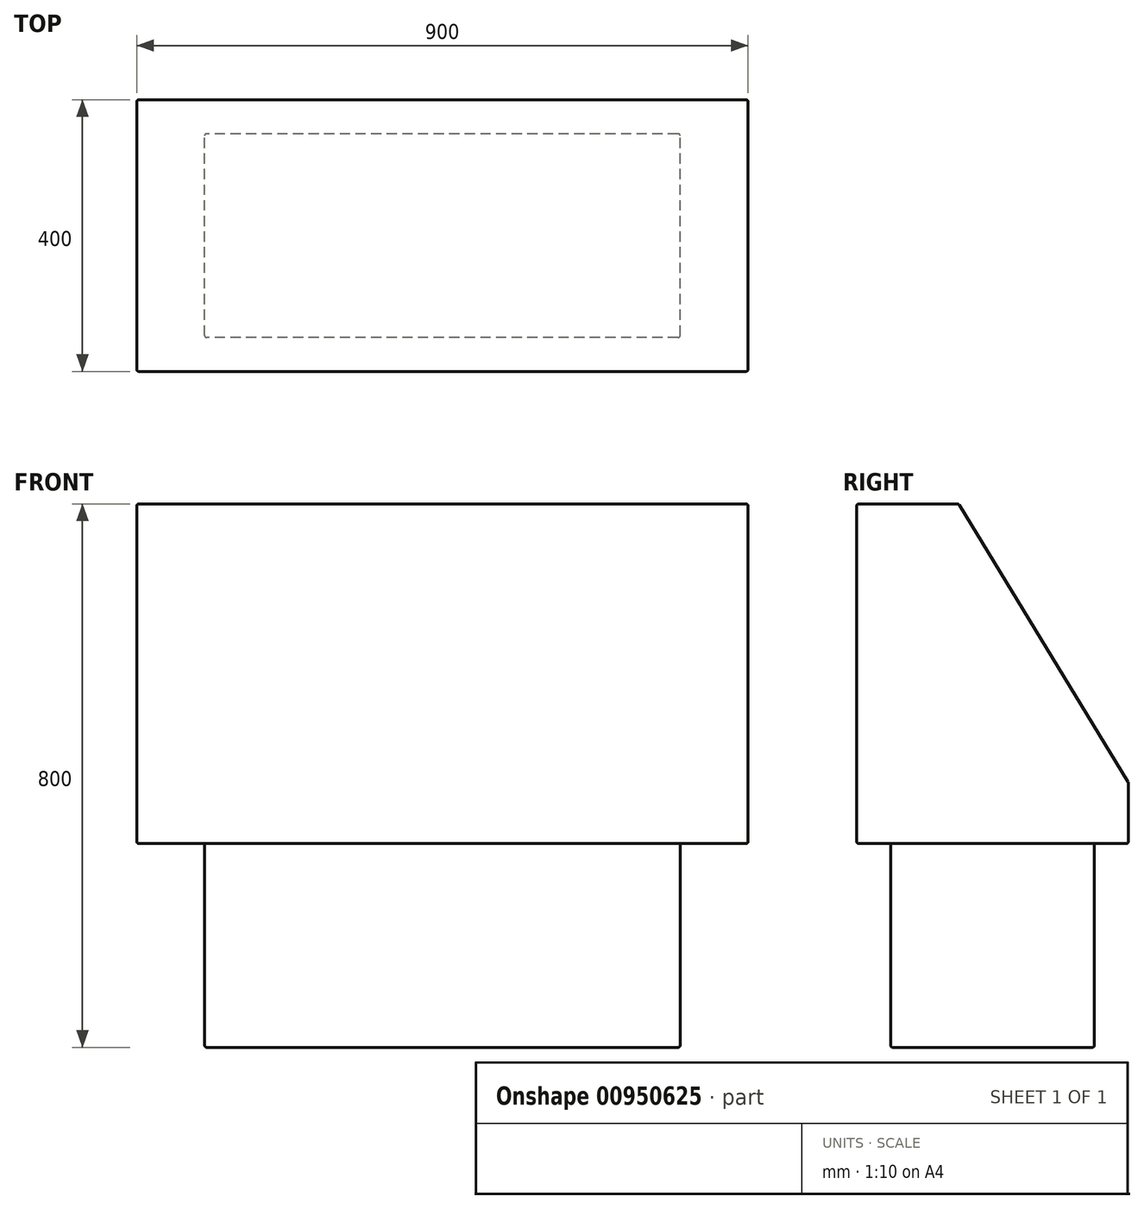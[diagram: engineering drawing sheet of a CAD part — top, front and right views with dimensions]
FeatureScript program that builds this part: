
annotation { "Feature Type Name" : "Feature", "Feature Type Description" : "" }
export const myFeature = defineFeature(function(context is Context, id is Id, definition is map)
    precondition{}
    {
        {
            var Q0;
            Q0=qCreatedBy(makeId("Top.planeOp"),FACE);
            var sketch = newSketch(context, id + "F0", { "sketchPlane" : qUnion([Q0])});
            skLineSegment(sketch, "E0.bottom", {"start": v(450, -200) * mm, "end": v(-450, -200) * mm});
            skLineSegment(sketch, "E0.top", {"start": v(450, 200) * mm, "end": v(-450, 200) * mm});
            skLineSegment(sketch, "E0.left", {"start": v(450, -200) * mm, "end": v(450, 200) * mm});
            skLineSegment(sketch, "E0.right", {"start": v(-450, -200) * mm, "end": v(-450, 200) * mm});
            skPoint(sketch, "E0.middle", {"position": v(0, 0) * mm});
            skLineSegment(sketch, "E1.bottom", {"start": v(350, -150) * mm, "end": v(-350, -150) * mm});
            skLineSegment(sketch, "E1.top", {"start": v(350, 150) * mm, "end": v(-350, 150) * mm});
            skLineSegment(sketch, "E1.left", {"start": v(350, -150) * mm, "end": v(350, 150) * mm});
            skLineSegment(sketch, "E1.right", {"start": v(-350, -150) * mm, "end": v(-350, 150) * mm});
            skSolve(sketch);
        }
        {
            var Q0;
            Q0=qCreatedBy(makeId("Right.planeOp"),FACE);
            var sketch = newSketch(context, id + "F1", { "sketchPlane" : qUnion([Q0])});
            skLineSegment(sketch, "E2", {"start": v(-200, 0) * mm, "end": v(-200, 500) * mm});
            skLineSegment(sketch, "E3", {"start": v(-200, 500) * mm, "end": v(-50, 500) * mm});
            skLineSegment(sketch, "E4", {"start": v(-50, 500) * mm, "end": v(200, 90) * mm});
            skLineSegment(sketch, "E5", {"start": v(200, 90) * mm, "end": v(200, 0) * mm});
            skLineSegment(sketch, "E6", {"start": v(200, 0) * mm, "end": v(-200, 0) * mm});
            skLineSegment(sketch, "E7.bottom", {"start": v(-150, 0) * mm, "end": v(150, 0) * mm});
            skLineSegment(sketch, "E7.top", {"start": v(-150, -300) * mm, "end": v(150, -300) * mm});
            skLineSegment(sketch, "E7.left", {"start": v(-150, 0) * mm, "end": v(-150, -300) * mm});
            skLineSegment(sketch, "E7.right", {"start": v(150, 0) * mm, "end": v(150, -300) * mm});
            skSolve(sketch);
        }
        {
            var Q0;
            Q0=sQuery(id+"F0.wireOp",VERTEX,"E0.bottom.start");
            var Q1;
            Q1=sQuery(id+"F0.wireOp",EDGE,"E0.bottom");
            cPlane(context, id + "F2", {"entities" : qUnion([Q0, Q1]), "cplaneType" : CPlaneType.LINE_POINT, "offset" : 25 * mm, "width" : 150 * mm, "height" : 150 * mm});
        }
        {
            var Q0;
            Q0=qCreatedBy(id+"F2.planeOp",FACE);
            var sketch = newSketch(context, id + "F3", { "sketchPlane" : qUnion([Q0])});
            skLineSegment(sketch, "E8.0", {"start": v(200, 0) * mm, "end": v(200, 500) * mm});
            skLineSegment(sketch, "E8.1", {"start": v(200, 500) * mm, "end": v(50, 500) * mm});
            skLineSegment(sketch, "E8.2", {"start": v(50, 500) * mm, "end": v(-200, 90) * mm});
            skLineSegment(sketch, "E8.3", {"start": v(-200, 90) * mm, "end": v(-200, 0) * mm});
            skLineSegment(sketch, "E8.4", {"start": v(-200, 0) * mm, "end": v(200, 0) * mm});
            skSolve(sketch);
        }
        {
            var Q0;
            Q0 = qSketchRegion(id + "F3", true);
            var Q1;
            Q1=sQuery(id+"F0.wireOp",VERTEX,"E0.top.end");
            extrude(context, id + "F4", {"entities" : qUnion([Q0]), "endBound" : BoundingType.UP_TO_VERTEX, "depth" : 25 * mm, "endBoundEntityVertex" : qUnion([Q1]), "offsetDistance" : 25 * mm});
        }
        {
            var Q0;
            Q0=makeQuery(id+"F4.opExtrude","SWEPT_FACE",FACE,{"disambiguationData":[OSD([sQuery(id+"F3.wireOp",EDGE,"E8.4")])]});
            var sketch = newSketch(context, id + "F5", { "sketchPlane" : qUnion([Q0])});
            skPoint(sketch, "E9.13", {"position": v(0, 0) * mm});
            skLineSegment(sketch, "E9.14", {"start": v(350, 150) * mm, "end": v(-350, 150) * mm});
            skLineSegment(sketch, "E9.15", {"start": v(350, -150) * mm, "end": v(-350, -150) * mm});
            skLineSegment(sketch, "E9.16", {"start": v(350, 150) * mm, "end": v(350, -150) * mm});
            skLineSegment(sketch, "E9.17", {"start": v(-350, 150) * mm, "end": v(-350, -150) * mm});
            skPoint(sketch, "E9.18", {"position": v(0, 0) * mm});
            skSolve(sketch);
        }
        {
            var Q0;
            Q0 = qSketchRegion(id + "F5", true);
            var Q1;
            Q1=sQuery(id+"F1.wireOp",VERTEX,"E7.top.start");
            extrude(context, id + "F6", {"entities" : qUnion([Q0]), "endBound" : BoundingType.UP_TO_VERTEX, "depth" : 25 * mm, "endBoundEntityVertex" : qUnion([Q1]), "offsetDistance" : 25 * mm});
        }
        {
            var Q0;
            Q0=makeQuery(id+"F4.opExtrude","SWEPT_EDGE",EDGE,{"disambiguationData":[OSD([sQuery(id+"F3.wireOp",EDGE,"E8.2"),sQuery(id+"F3.wireOp",EDGE,"E8.3")])]});
            var Q1;
            Q1=makeQuery(id+"F4.opExtrude","SWEPT_EDGE",EDGE,{"disambiguationData":[OSD([sQuery(id+"F3.wireOp",EDGE,"E8.1"),sQuery(id+"F3.wireOp",EDGE,"E8.2")])]});
            var Q2;
            Q2=makeQuery(id+"F4.opExtrude","SWEPT_EDGE",EDGE,{"disambiguationData":[OSD([sQuery(id+"F3.wireOp",EDGE,"E8.0"),sQuery(id+"F3.wireOp",EDGE,"E8.1")])]});
            var Q3;
            Q3=makeQuery(id+"F4.opExtrude","CAP_EDGE",EDGE,{"disambiguationData":[OSD([sQuery(id+"F3.wireOp",EDGE,"E8.4")])],"isStart":true});
            var Q4;
            Q4=makeQuery(id+"F4.opExtrude","SWEPT_EDGE",EDGE,{"disambiguationData":[OSD([sQuery(id+"F3.wireOp",EDGE,"E8.3"),sQuery(id+"F3.wireOp",EDGE,"E8.4")])]});
            var Q5;
            Q5=makeQuery(id+"F4.opExtrude","CAP_EDGE",EDGE,{"disambiguationData":[OSD([sQuery(id+"F3.wireOp",EDGE,"E8.1")])],"isStart":true});
            var Q6;
            Q6=makeQuery(id+"F4.opExtrude","CAP_EDGE",EDGE,{"disambiguationData":[OSD([sQuery(id+"F3.wireOp",EDGE,"E8.1")])],"isStart":false});
            var Q7;
            Q7=makeQuery(id+"F4.opExtrude","CAP_EDGE",EDGE,{"disambiguationData":[OSD([sQuery(id+"F3.wireOp",EDGE,"E8.2")])],"isStart":true});
            var Q8;
            Q8=makeQuery(id+"F4.opExtrude","SWEPT_EDGE",EDGE,{"disambiguationData":[OSD([sQuery(id+"F3.wireOp",EDGE,"E8.0"),sQuery(id+"F3.wireOp",EDGE,"E8.4")])]});
            var Q9;
            Q9=makeQuery(id+"F4.opExtrude","CAP_EDGE",EDGE,{"disambiguationData":[OSD([sQuery(id+"F3.wireOp",EDGE,"E8.4")])],"isStart":false});
            var Q10;
            Q10=makeQuery(id+"F4.opExtrude","CAP_EDGE",EDGE,{"disambiguationData":[OSD([sQuery(id+"F3.wireOp",EDGE,"E8.0")])],"isStart":true});
            var Q11;
            Q11=makeQuery(id+"F4.opExtrude","CAP_EDGE",EDGE,{"disambiguationData":[OSD([sQuery(id+"F3.wireOp",EDGE,"E8.0")])],"isStart":false});
            var Q12;
            Q12=makeQuery(id+"F4.opExtrude","CAP_EDGE",EDGE,{"disambiguationData":[OSD([sQuery(id+"F3.wireOp",EDGE,"E8.2")])],"isStart":false});
            var Q13;
            Q13=makeQuery(id+"F4.opExtrude","CAP_EDGE",EDGE,{"disambiguationData":[OSD([sQuery(id+"F3.wireOp",EDGE,"E8.3")])],"isStart":true});
            var Q14;
            Q14=makeQuery(id+"F4.opExtrude","CAP_EDGE",EDGE,{"disambiguationData":[OSD([sQuery(id+"F3.wireOp",EDGE,"E8.3")])],"isStart":false});
            fillet(context, id + "F7", {"entities" : qUnion([Q0, Q1, Q2, Q3, Q4, Q5, Q6, Q7, Q8, Q9, Q10, Q11, Q12, Q13, Q14]), "radius" : 3 * mm, "tangentPropagation" : true, "allowEdgeOverflow" : false});
        }
        {
            var Q0;
            Q0=makeQuery(id+"F6.opExtrude","CAP_EDGE",EDGE,{"disambiguationData":[OSD([sQuery(id+"F5.wireOp",EDGE,"E9.14")])],"isStart":true});
            var Q1;
            Q1=makeQuery(id+"F6.opExtrude","CAP_EDGE",EDGE,{"disambiguationData":[OSD([sQuery(id+"F5.wireOp",EDGE,"E9.17")])],"isStart":true});
            var Q2;
            Q2=makeQuery(id+"F6.opExtrude","CAP_EDGE",EDGE,{"disambiguationData":[OSD([sQuery(id+"F5.wireOp",EDGE,"E9.16")])],"isStart":true});
            var Q3;
            Q3=makeQuery(id+"F6.opExtrude","CAP_EDGE",EDGE,{"disambiguationData":[OSD([sQuery(id+"F5.wireOp",EDGE,"E9.16")])],"isStart":false});
            var Q4;
            Q4=makeQuery(id+"F6.opExtrude","CAP_EDGE",EDGE,{"disambiguationData":[OSD([sQuery(id+"F5.wireOp",EDGE,"E9.17")])],"isStart":false});
            var Q5;
            Q5=makeQuery(id+"F6.opExtrude","SWEPT_EDGE",EDGE,{"disambiguationData":[OSD([sQuery(id+"F5.wireOp",EDGE,"E9.14"),sQuery(id+"F5.wireOp",EDGE,"E9.16")])]});
            var Q6;
            Q6=makeQuery(id+"F6.opExtrude","SWEPT_EDGE",EDGE,{"disambiguationData":[OSD([sQuery(id+"F5.wireOp",EDGE,"E9.15"),sQuery(id+"F5.wireOp",EDGE,"E9.16")])]});
            var Q7;
            Q7=makeQuery(id+"F6.opExtrude","CAP_EDGE",EDGE,{"disambiguationData":[OSD([sQuery(id+"F5.wireOp",EDGE,"E9.14")])],"isStart":false});
            var Q8;
            Q8=makeQuery(id+"F6.opExtrude","CAP_EDGE",EDGE,{"disambiguationData":[OSD([sQuery(id+"F5.wireOp",EDGE,"E9.15")])],"isStart":true});
            var Q9;
            Q9=makeQuery(id+"F6.opExtrude","SWEPT_EDGE",EDGE,{"disambiguationData":[OSD([sQuery(id+"F5.wireOp",EDGE,"E9.15"),sQuery(id+"F5.wireOp",EDGE,"E9.17")])]});
            var Q10;
            Q10=makeQuery(id+"F6.opExtrude","CAP_EDGE",EDGE,{"disambiguationData":[OSD([sQuery(id+"F5.wireOp",EDGE,"E9.15")])],"isStart":false});
            var Q11;
            Q11=makeQuery(id+"F6.opExtrude","SWEPT_EDGE",EDGE,{"disambiguationData":[OSD([sQuery(id+"F5.wireOp",EDGE,"E9.14"),sQuery(id+"F5.wireOp",EDGE,"E9.17")])]});
            fillet(context, id + "F8", {"entities" : qUnion([Q0, Q1, Q2, Q3, Q4, Q5, Q6, Q7, Q8, Q9, Q10, Q11]), "radius" : 3 * mm, "tangentPropagation" : true, "allowEdgeOverflow" : false});
        }
    });
